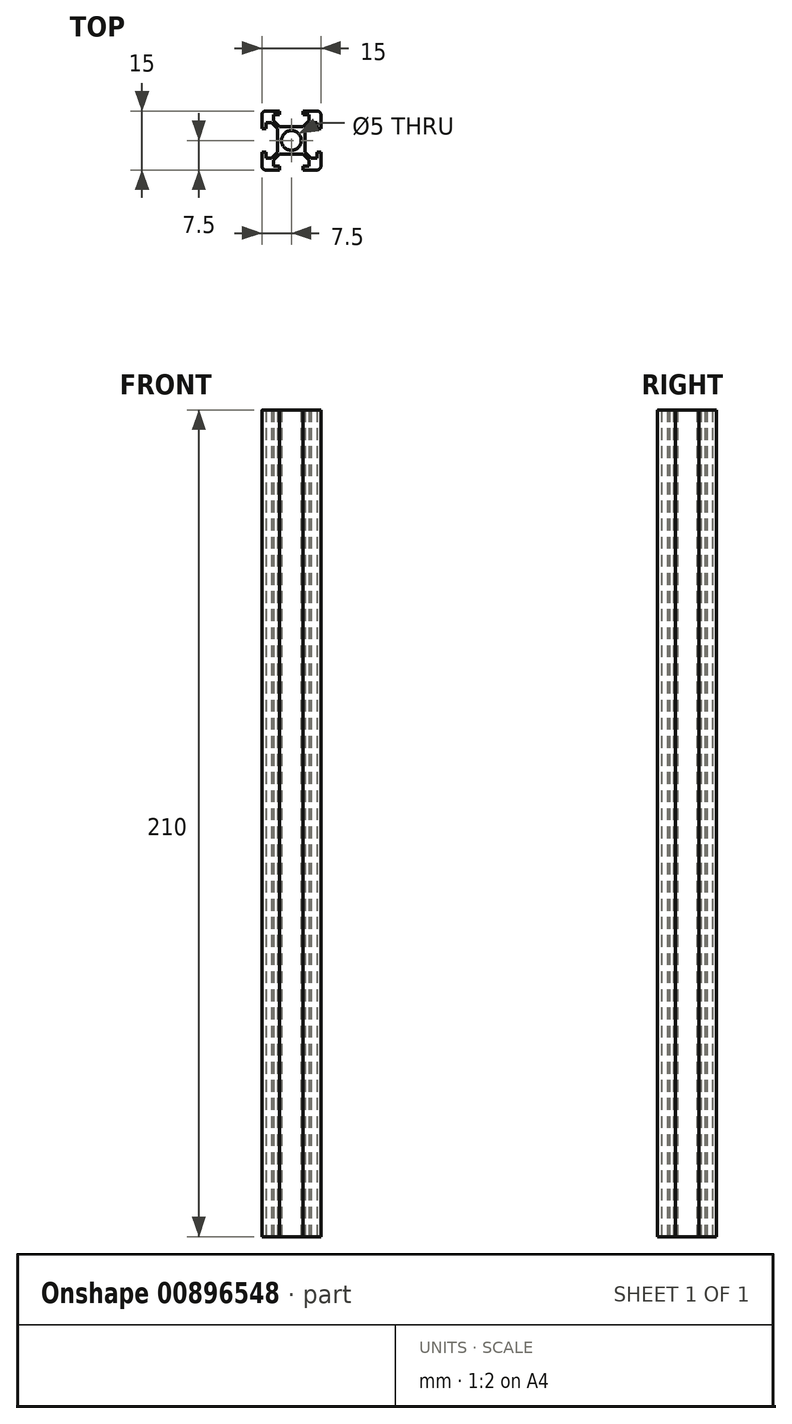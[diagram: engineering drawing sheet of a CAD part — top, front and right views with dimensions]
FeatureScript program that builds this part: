
annotation { "Feature Type Name" : "Feature", "Feature Type Description" : "" }
export const myFeature = defineFeature(function(context is Context, id is Id, definition is map)
    precondition{}
    {
        {
            assignVariable(context, id + "F0", {"name" : "height", "anyValue" : 210});
        }
        {
            var Q0;
            Q0=qCreatedBy(makeId("Top.planeOp"),FACE);
            var sketch = newSketch(context, id + "F1", { "sketchPlane" : qUnion([Q0])});
            skCircle(sketch, "E0", {"center": v(0, 0) * mm, "radius": 2.5 * mm});
            skLineSegment(sketch, "E1.bottom", {"start": v(6.5, 7.5) * mm, "end": v(3, 7.5) * mm});
            skLineSegment(sketch, "E1.top", {"start": v(6.5, -7.5) * mm, "end": v(3, -7.5) * mm});
            skLineSegment(sketch, "E1.left", {"start": v(7.5, 6.5) * mm, "end": v(7.5, 3) * mm});
            skLineSegment(sketch, "E1.right", {"start": v(-7.5, 6.5) * mm, "end": v(-7.5, 3) * mm});
            skPoint(sketch, "E2.visualSharp", {"position": v(-7.5, 7.5) * mm});
            skArc(sketch, "E2.filletArc", {"start": v(-6.5, 7.5) * mm, "mid": v(-7.2, 7.2) * mm, "end": v(-7.5, 6.5) * mm});
            skPoint(sketch, "E3.visualSharp", {"position": v(7.5, 7.5) * mm});
            skArc(sketch, "E3.filletArc", {"start": v(7.5, 6.5) * mm, "mid": v(7.2, 7.2) * mm, "end": v(6.5, 7.5) * mm});
            skPoint(sketch, "E4.visualSharp", {"position": v(7.5, -7.5) * mm});
            skArc(sketch, "E4.filletArc", {"start": v(6.5, -7.5) * mm, "mid": v(7.2, -7.2) * mm, "end": v(7.5, -6.5) * mm});
            skPoint(sketch, "E5.visualSharp", {"position": v(-7.5, -7.5) * mm});
            skArc(sketch, "E5.filletArc", {"start": v(-7.5, -6.5) * mm, "mid": v(-7.2, -7.2) * mm, "end": v(-6.5, -7.5) * mm});
            skLineSegment(sketch, "E6", {"start": v(-3, 7.5) * mm, "end": v(-3, 6.5) * mm});
            skLineSegment(sketch, "E7", {"start": v(3, 7.5) * mm, "end": v(3, 6.5) * mm});
            skLineSegment(sketch, "E8", {"start": v(-4.5, 6.5) * mm, "end": v(-4.5, 5) * mm});
            skLineSegment(sketch, "E9", {"start": v(4.5, 5) * mm, "end": v(4.5, 6.5) * mm});
            skLineSegment(sketch, "E10", {"start": v(4.5, 6.5) * mm, "end": v(3, 6.5) * mm});
            skLineSegment(sketch, "E11", {"start": v(-3, 3.5) * mm, "end": v(3, 3.5) * mm});
            skLineSegment(sketch, "E12", {"start": v(3, 3.5) * mm, "end": v(4.5, 5) * mm});
            skLineSegment(sketch, "E13", {"start": v(-3, 3.5) * mm, "end": v(-4.5, 5) * mm});
            skLineSegment(sketch, "E14.trimOffspring", {"start": v(-3, 6.5) * mm, "end": v(-4.5, 6.5) * mm});
            skLineSegment(sketch, "E15", {"start": v(-3, -7.5) * mm, "end": v(-3, -6.5) * mm});
            skLineSegment(sketch, "E16", {"start": v(-3, -6.5) * mm, "end": v(-4.5, -6.5) * mm});
            skLineSegment(sketch, "E17", {"start": v(-4.5, -6.5) * mm, "end": v(-4.5, -5) * mm});
            skLineSegment(sketch, "E18", {"start": v(-4.5, -5) * mm, "end": v(-3, -3.5) * mm});
            skLineSegment(sketch, "E19", {"start": v(-3, -3.5) * mm, "end": v(3, -3.5) * mm});
            skLineSegment(sketch, "E20", {"start": v(3, -3.5) * mm, "end": v(4.5, -5) * mm});
            skLineSegment(sketch, "E21", {"start": v(4.5, -5) * mm, "end": v(4.5, -6.5) * mm});
            skLineSegment(sketch, "E22", {"start": v(4.5, -6.5) * mm, "end": v(3, -6.5) * mm});
            skLineSegment(sketch, "E23", {"start": v(3, -6.5) * mm, "end": v(3, -7.5) * mm});
            skPoint(sketch, "E24", {"position": v(0, 7.5) * mm});
            skPoint(sketch, "E25", {"position": v(0, -7.5) * mm});
            skPoint(sketch, "E26", {"position": v(7.5, 0) * mm});
            skPoint(sketch, "E27", {"position": v(-7.5, 0) * mm});
            skLineSegment(sketch, "E28", {"start": v(7.5, 3) * mm, "end": v(6.5, 3) * mm});
            skLineSegment(sketch, "E29", {"start": v(6.5, 3) * mm, "end": v(6.5, 4.5) * mm});
            skLineSegment(sketch, "E30", {"start": v(6.5, 4.5) * mm, "end": v(5, 4.5) * mm});
            skLineSegment(sketch, "E31", {"start": v(5, 4.5) * mm, "end": v(3.5, 3) * mm});
            skLineSegment(sketch, "E32", {"start": v(3.5, 3) * mm, "end": v(3.5, -3) * mm});
            skLineSegment(sketch, "E33", {"start": v(3.5, -3) * mm, "end": v(5, -4.5) * mm});
            skLineSegment(sketch, "E34", {"start": v(5, -4.5) * mm, "end": v(6.5, -4.5) * mm});
            skLineSegment(sketch, "E35", {"start": v(6.5, -4.5) * mm, "end": v(6.5, -3) * mm});
            skLineSegment(sketch, "E36", {"start": v(6.5, -3) * mm, "end": v(7.5, -3) * mm});
            skLineSegment(sketch, "E37.trimOffspring", {"start": v(-3, 7.5) * mm, "end": v(-6.5, 7.5) * mm});
            skLineSegment(sketch, "E38.trimOffspring", {"start": v(7.5, -3) * mm, "end": v(7.5, -6.5) * mm});
            skLineSegment(sketch, "E39.trimOffspring", {"start": v(-3, -7.5) * mm, "end": v(-6.5, -7.5) * mm});
            skLineSegment(sketch, "E40", {"start": v(-7.5, 3) * mm, "end": v(-6.5, 3) * mm});
            skLineSegment(sketch, "E41", {"start": v(-6.5, 3) * mm, "end": v(-6.5, 4.5) * mm});
            skLineSegment(sketch, "E42", {"start": v(-6.5, 4.5) * mm, "end": v(-5, 4.5) * mm});
            skLineSegment(sketch, "E43", {"start": v(-5, 4.5) * mm, "end": v(-3.5, 3) * mm});
            skLineSegment(sketch, "E44", {"start": v(-3.5, 3) * mm, "end": v(-3.5, -3) * mm});
            skLineSegment(sketch, "E45", {"start": v(-3.5, -3) * mm, "end": v(-5, -4.5) * mm});
            skLineSegment(sketch, "E46", {"start": v(-5, -4.5) * mm, "end": v(-6.5, -4.5) * mm});
            skLineSegment(sketch, "E47", {"start": v(-6.5, -4.5) * mm, "end": v(-6.5, -3) * mm});
            skLineSegment(sketch, "E48", {"start": v(-6.5, -3) * mm, "end": v(-7.5, -3) * mm});
            skLineSegment(sketch, "E49.trimOffspring", {"start": v(-7.5, -3) * mm, "end": v(-7.5, -6.5) * mm});
            skSolve(sketch);
        }
        {
            var Q0;
            Q0=qSketchRegion(id+"F1",true);
            extrude(context, id + "F2", {"entities" : qUnion([Q0]), "depth" : (getVariable(context, 'height')) * mm, "offsetDistance" : 25 * mm});
        }
    });
